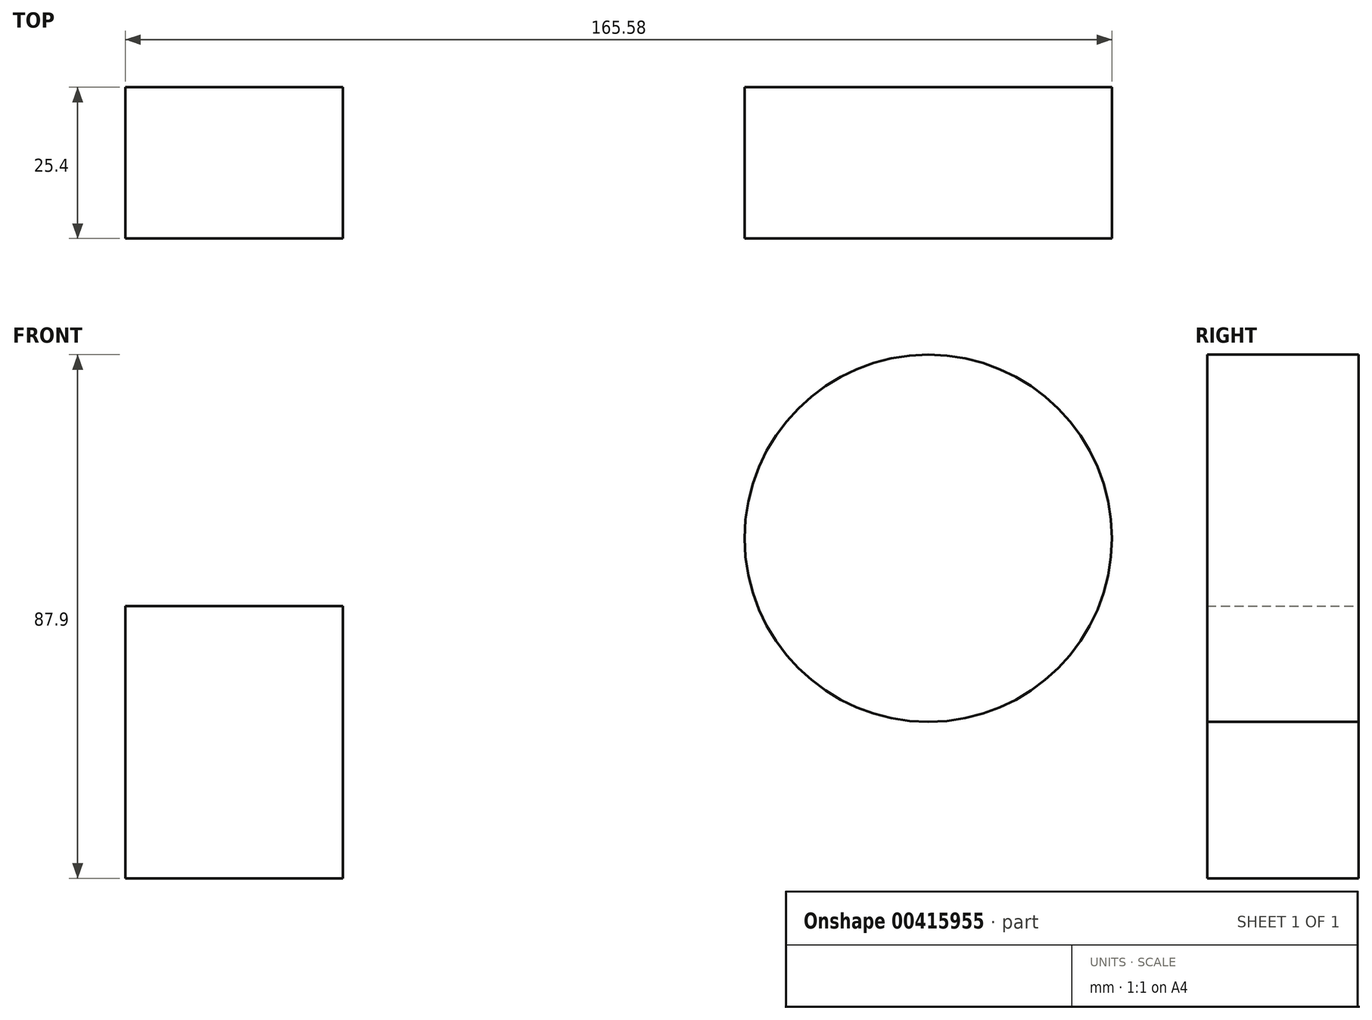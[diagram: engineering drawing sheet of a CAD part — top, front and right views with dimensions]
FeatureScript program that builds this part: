
annotation { "Feature Type Name" : "Feature", "Feature Type Description" : "" }
export const myFeature = defineFeature(function(context is Context, id is Id, definition is map)
    precondition{}
    {
        {
            var Q0;
            Q0=qCreatedBy(makeId("Front.planeOp"),FACE);
            var sketch = newSketch(context, id + "F0", { "sketchPlane" : qUnion([Q0])});
            skLineSegment(sketch, "E0.bottom", {"start": v(-65.63, 45.72) * mm, "end": v(-29.13, 45.72) * mm});
            skLineSegment(sketch, "E0.top", {"start": v(-65.63, 0) * mm, "end": v(-29.13, 0) * mm});
            skLineSegment(sketch, "E0.left", {"start": v(-65.63, 45.72) * mm, "end": v(-65.63, 0) * mm});
            skLineSegment(sketch, "E0.right", {"start": v(-29.13, 45.72) * mm, "end": v(-29.13, 0) * mm});
            skSolve(sketch);
        }
        {
            var Q0;
            Q0=makeQuery(id+"F0.imprint","IMPRINT",FACE,{"disambiguationData":[TD([[makeQuery(id+"F0.imprint","IMPRINT",EDGE,{"derivedFrom":sQuery(id+"F0.wireOp",EDGE,"E0.bottom")}),-1.0]])]});
            extrude(context, id + "F1", {"entities" : qUnion([Q0]), "depth" : 25.4 * mm});
        }
        {
            var Q0;
            Q0=qCreatedBy(makeId("Front.planeOp"),FACE);
            var sketch = newSketch(context, id + "F2", { "sketchPlane" : qUnion([Q0])});
            skCircle(sketch, "E1", {"center": v(69.12, 57.07) * mm, "radius": 30.83 * mm});
            skSolve(sketch);
        }
        {
            var Q0;
            Q0=makeQuery(id+"F2.imprint","IMPRINT",FACE,{"disambiguationData":[TD([[makeQuery(id+"F2.imprint","IMPRINT",EDGE,{"derivedFrom":sQuery(id+"F2.wireOp",EDGE,"E1")}),1.0]])]});
            extrude(context, id + "F3", {"entities" : qUnion([Q0]), "depth" : 25.4 * mm});
        }
    });
